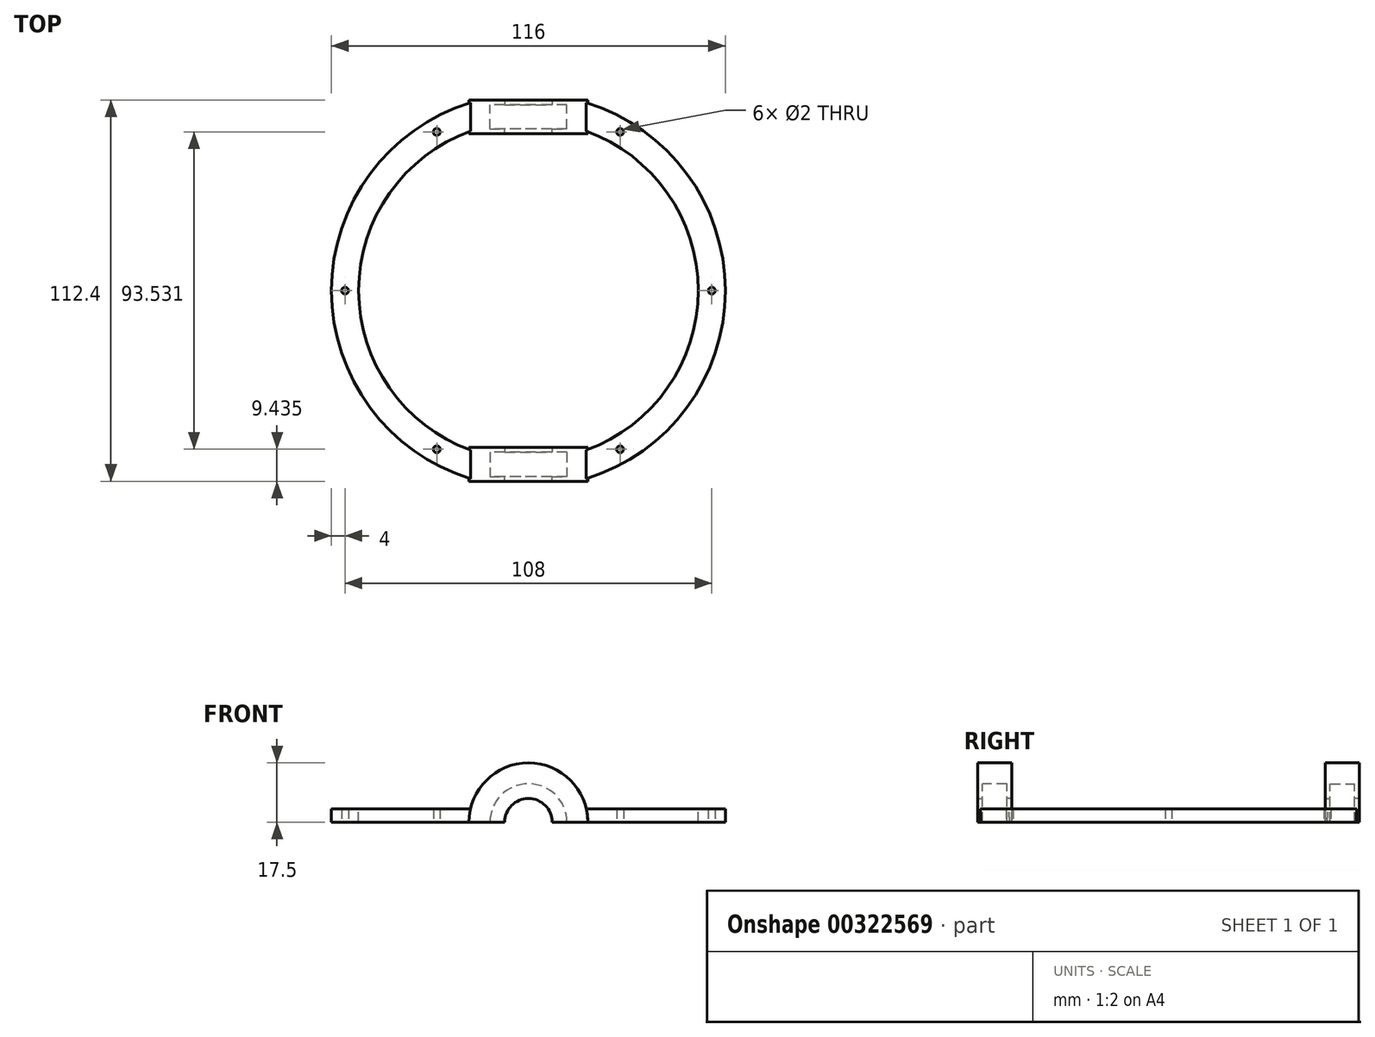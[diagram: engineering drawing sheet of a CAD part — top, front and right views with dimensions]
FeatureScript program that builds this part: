
annotation { "Feature Type Name" : "Feature", "Feature Type Description" : "" }
export const myFeature = defineFeature(function(context is Context, id is Id, definition is map)
    precondition{}
    {
        {
            var Q0;
            Q0=qCreatedBy(makeId("Top.planeOp"),FACE);
            var sketch = newSketch(context, id + "F0", { "sketchPlane" : qUnion([Q0])});
            skCircle(sketch, "E0", {"center": v(0, 0) * mm, "radius": 50 * mm});
            skCircle(sketch, "E1", {"center": v(0, 0) * mm, "radius": 58 * mm});
            skSolve(sketch);
        }
        {
            var Q0;
            Q0=qSketchRegion(id+"F0",true);
            extrude(context, id + "F1", {"entities" : qUnion([Q0]), "depth" : 4 * mm, "hasSecondDirection" : true, "secondDirectionOppositeDirection" : true, "secondDirectionDepth" : 4 * mm});
        }
        {
            var Q0;
            Q0=qCreatedBy(makeId("Front.planeOp"),FACE);
            cPlane(context, id + "F2", {"entities" : qUnion([Q0]), "cplaneType" : CPlaneType.OFFSET, "offset" : 54.8 * mm, "width" : 150 * mm, "height" : 150 * mm});
        }
        {
            var Q0;
            Q0=qCreatedBy(id+"F2.planeOp",FACE);
            var sketch = newSketch(context, id + "F3", { "sketchPlane" : qUnion([Q0])});
            skCircle(sketch, "E2", {"center": v(0, 0) * mm, "radius": 11.35 * mm});
            skCircle(sketch, "E3", {"center": v(0, 0) * mm, "radius": 17.5 * mm});
            skSolve(sketch);
        }
        {
            var Q0;
            Q0=makeQuery(id+"F3.imprint","IMPRINT",FACE,{"disambiguationData":[TD([[makeQuery(id+"F3.imprint","IMPRINT",EDGE,{"derivedFrom":sQuery(id+"F3.wireOp",EDGE,"E2")}),1.0]])]});
            var Q1;
            Q1=makeQuery(id+"F3.imprint","IMPRINT",FACE,{"disambiguationData":[TD([[makeQuery(id+"F3.imprint","IMPRINT",EDGE,{"derivedFrom":sQuery(id+"F3.wireOp",EDGE,"E2")}),-1.0]])]});
            extrude(context, id + "F4", {"entities" : qUnion([Q0, Q1]), "operationType" : NewBodyOperationType.REMOVE, "oppositeDirection" : true, "depth" : 25 * mm, "hasSecondDirection" : true, "secondDirectionOppositeDirection" : false, "secondDirectionDepth" : 25 * mm});
        }
        {
            var Q0;
            Q0=makeQuery(id+"F3.imprint","IMPRINT",FACE,{"disambiguationData":[TD([[makeQuery(id+"F3.imprint","IMPRINT",EDGE,{"derivedFrom":sQuery(id+"F3.wireOp",EDGE,"E2")}),-1.0]])]});
            extrude(context, id + "F5", {"entities" : qUnion([Q0]), "operationType" : NewBodyOperationType.ADD, "oppositeDirection" : true, "depth" : 7.2 * mm});
        }
        {
            var Q0;
            Q0=makeQuery(id+"F5.opExtrude","CAP_FACE",FACE,{"disambiguationData":[OSD([sQuery(id+"F3.wireOp",EDGE,"E2"),sQuery(id+"F3.wireOp",EDGE,"E3")])],"isStart":true});
            var sketch = newSketch(context, id + "F6", { "sketchPlane" : qUnion([Q0])});
            skCircle(sketch, "E4", {"center": v(0, 0) * mm, "radius": 7 * mm});
            skCircle(sketch, "E5", {"center": v(0, 0) * mm, "radius": 17.5 * mm});
            skSolve(sketch);
        }
        {
            var Q0;
            Q0=makeQuery(id+"F6.imprint","IMPRINT",FACE,{"disambiguationData":[TD([[makeQuery(id+"F6.imprint","IMPRINT",EDGE,{"derivedFrom":sQuery(id+"F6.wireOp",EDGE,"E4")}),-1.0]])]});
            var Q1;
            Q1=makeQuery(id+"F6.imprint","IMPRINT",FACE,{"disambiguationData":[TD([[makeQuery(id+"F6.imprint","IMPRINT",EDGE,{"derivedFrom":sQuery(id+"F6.wireOp",EDGE,"E5")}),1.0]])]});
            extrude(context, id + "F7", {"entities" : qUnion([Q0, Q1]), "operationType" : NewBodyOperationType.ADD, "depth" : 1.4 * mm});
        }
        {
            var Q0;
            Q0=makeQuery(id+"F5.opExtrude","CAP_FACE",FACE,{"disambiguationData":[OSD([sQuery(id+"F3.wireOp",EDGE,"E2"),sQuery(id+"F3.wireOp",EDGE,"E3")])],"isStart":false});
            var sketch = newSketch(context, id + "F8", { "sketchPlane" : qUnion([Q0])});
            skCircle(sketch, "E6", {"center": v(0, 0) * mm, "radius": 7 * mm});
            skCircle(sketch, "E7", {"center": v(0, 0) * mm, "radius": 17.5 * mm});
            skSolve(sketch);
        }
        {
            var Q0;
            Q0=makeQuery(id+"F8.imprint","IMPRINT",FACE,{"disambiguationData":[TD([[makeQuery(id+"F8.imprint","IMPRINT",EDGE,{"derivedFrom":sQuery(id+"F8.wireOp",EDGE,"E7")}),-1.0]])]});
            var Q1;
            Q1=makeQuery(id+"F8.imprint","IMPRINT",FACE,{"disambiguationData":[TD([[makeQuery(id+"F8.imprint","IMPRINT",EDGE,{"derivedFrom":sQuery(id+"F8.wireOp",EDGE,"E6")}),-1.0]])]});
            extrude(context, id + "F9", {"entities" : qUnion([Q0, Q1]), "operationType" : NewBodyOperationType.ADD, "depth" : 1.4 * mm});
        }
        {
            var Q0;
            Q0=qCreatedBy(makeId("Front.planeOp"),FACE);
            cPlane(context, id + "F10", {"entities" : qUnion([Q0]), "cplaneType" : CPlaneType.OFFSET, "offset" : 54.8 * mm, "oppositeDirection" : true, "width" : 150 * mm, "height" : 150 * mm});
        }
        {
            var Q0;
            Q0=qCreatedBy(id+"F10.planeOp",FACE);
            var sketch = newSketch(context, id + "F11", { "sketchPlane" : qUnion([Q0])});
            skCircle(sketch, "E8", {"center": v(0, 0) * mm, "radius": 17.5 * mm});
            skCircle(sketch, "E9", {"center": v(0, 0) * mm, "radius": 11.35 * mm});
            skSolve(sketch);
        }
        {
            var Q0;
            Q0=makeQuery(id+"F11.imprint","IMPRINT",FACE,{"disambiguationData":[TD([[makeQuery(id+"F11.imprint","IMPRINT",EDGE,{"derivedFrom":sQuery(id+"F11.wireOp",EDGE,"E8")}),1.0]])]});
            var Q1;
            Q1=makeQuery(id+"F11.imprint","IMPRINT",FACE,{"disambiguationData":[TD([[makeQuery(id+"F11.imprint","IMPRINT",EDGE,{"derivedFrom":sQuery(id+"F11.wireOp",EDGE,"E9")}),1.0]])]});
            extrude(context, id + "F12", {"entities" : qUnion([Q0, Q1]), "operationType" : NewBodyOperationType.REMOVE, "depth" : 25 * mm, "hasSecondDirection" : true, "secondDirectionOppositeDirection" : true, "secondDirectionDepth" : 25 * mm});
        }
        {
            var Q0;
            Q0=makeQuery(id+"F11.imprint","IMPRINT",FACE,{"disambiguationData":[TD([[makeQuery(id+"F11.imprint","IMPRINT",EDGE,{"derivedFrom":sQuery(id+"F11.wireOp",EDGE,"E8")}),1.0]])]});
            extrude(context, id + "F13", {"entities" : qUnion([Q0]), "operationType" : NewBodyOperationType.ADD, "depth" : 7.2 * mm});
        }
        {
            var Q0;
            Q0=makeQuery(id+"F13.opExtrude","CAP_FACE",FACE,{"disambiguationData":[OSD([sQuery(id+"F11.wireOp",EDGE,"E8"),sQuery(id+"F11.wireOp",EDGE,"E9")])],"isStart":true});
            var sketch = newSketch(context, id + "F14", { "sketchPlane" : qUnion([Q0])});
            skCircle(sketch, "E10", {"center": v(0, 0) * mm, "radius": 7 * mm});
            skCircle(sketch, "E11", {"center": v(0, 0) * mm, "radius": 17.5 * mm});
            skSolve(sketch);
        }
        {
            var Q0;
            Q0=makeQuery(id+"F14.imprint","IMPRINT",FACE,{"disambiguationData":[TD([[makeQuery(id+"F14.imprint","IMPRINT",EDGE,{"derivedFrom":makeQuery(id+"F13.opExtrude","CAP_EDGE",EDGE,{"disambiguationData":[OSD([sQuery(id+"F11.wireOp",EDGE,"E9")])],"isStart":true})}),1.0]])]});
            var Q1;
            Q1=makeQuery(id+"F14.imprint","IMPRINT",FACE,{"disambiguationData":[TD([[makeQuery(id+"F14.imprint","IMPRINT",EDGE,{"derivedFrom":sQuery(id+"F14.wireOp",EDGE,"E10")}),-1.0]])]});
            extrude(context, id + "F15", {"entities" : qUnion([Q0, Q1]), "operationType" : NewBodyOperationType.ADD, "depth" : 1.4 * mm});
        }
        {
            var Q0;
            Q0=makeQuery(id+"F13.opExtrude","CAP_FACE",FACE,{"disambiguationData":[OSD([sQuery(id+"F11.wireOp",EDGE,"E8"),sQuery(id+"F11.wireOp",EDGE,"E9")])],"isStart":false});
            var sketch = newSketch(context, id + "F16", { "sketchPlane" : qUnion([Q0])});
            skCircle(sketch, "E12", {"center": v(0, 0) * mm, "radius": 7 * mm});
            skCircle(sketch, "E13", {"center": v(0, 0) * mm, "radius": 17.5 * mm});
            skSolve(sketch);
        }
        {
            var Q0;
            Q0=makeQuery(id+"F16.imprint","IMPRINT",FACE,{"disambiguationData":[TD([[makeQuery(id+"F16.imprint","IMPRINT",EDGE,{"derivedFrom":sQuery(id+"F16.wireOp",EDGE,"E12")}),-1.0]])]});
            var Q1;
            Q1=makeQuery(id+"F16.imprint","IMPRINT",FACE,{"disambiguationData":[TD([[makeQuery(id+"F16.imprint","IMPRINT",EDGE,{"derivedFrom":sQuery(id+"F16.wireOp",EDGE,"E13")}),1.0]])]});
            extrude(context, id + "F17", {"entities" : qUnion([Q0, Q1]), "operationType" : NewBodyOperationType.ADD, "depth" : 1.4 * mm});
        }
        {
            var Q0;
            Q0=makeQuery(id+"F12.boolean.opBoolean","SPLIT",FACE,{"disambiguationData":[OD(0.0)],"derivedFrom":makeQuery(id+"F1.opExtrude","CAP_FACE",FACE,{"disambiguationData":[OSD([sQuery(id+"F0.wireOp",EDGE,"E0"),sQuery(id+"F0.wireOp",EDGE,"E1")])],"isStart":false})});
            var sketch = newSketch(context, id + "F18", { "sketchPlane" : qUnion([Q0])});
            skLineSegment(sketch, "E14", {"start": v(0, 0) * mm, "end": v(-50, 0) * mm, "construction": true});
            skLineSegment(sketch, "E15", {"start": v(-50, 0) * mm, "end": v(-58, 0) * mm, "construction": true});
            skCircle(sketch, "E16", {"center": v(-54, 0) * mm, "radius": 3 * mm});
            skCircle(sketch, "E17", {"center": v(-54, 0) * mm, "radius": 1.5 * mm});
            skCircle(sketch, "E18", {"center": v(-54, 0) * mm, "radius": 1 * mm});
            skCircle(sketch, "E19.1.0", {"center": v(-27, -46.77) * mm, "radius": 3 * mm});
            skCircle(sketch, "E19.1.1", {"center": v(-27, -46.77) * mm, "radius": 1.5 * mm});
            skCircle(sketch, "E19.1.2", {"center": v(-27, -46.77) * mm, "radius": 1 * mm});
            skCircle(sketch, "E19.2.0", {"center": v(27, -46.77) * mm, "radius": 3 * mm});
            skCircle(sketch, "E19.2.1", {"center": v(27, -46.77) * mm, "radius": 1.5 * mm});
            skCircle(sketch, "E19.2.2", {"center": v(27, -46.77) * mm, "radius": 1 * mm});
            skCircle(sketch, "E19.3.0", {"center": v(54, 0) * mm, "radius": 3 * mm});
            skCircle(sketch, "E19.3.1", {"center": v(54, 0) * mm, "radius": 1.5 * mm});
            skCircle(sketch, "E19.3.2", {"center": v(54, 0) * mm, "radius": 1 * mm});
            skCircle(sketch, "E19.4.0", {"center": v(27, 46.77) * mm, "radius": 3 * mm});
            skCircle(sketch, "E19.4.1", {"center": v(27, 46.77) * mm, "radius": 1.5 * mm});
            skCircle(sketch, "E19.4.2", {"center": v(27, 46.77) * mm, "radius": 1 * mm});
            skCircle(sketch, "E19.5.0", {"center": v(-27, 46.77) * mm, "radius": 3 * mm});
            skCircle(sketch, "E19.5.1", {"center": v(-27, 46.77) * mm, "radius": 1.5 * mm});
            skCircle(sketch, "E19.5.2", {"center": v(-27, 46.77) * mm, "radius": 1 * mm});
            skPoint(sketch, "E19.center", {"position": v(0, 0) * mm});
            skSolve(sketch);
        }
        {
            var Q0;
            Q0=makeQuery(id+"F18.imprint","IMPRINT",FACE,{"disambiguationData":[TD([[makeQuery(id+"F18.imprint","IMPRINT",EDGE,{"derivedFrom":sQuery(id+"F18.wireOp",EDGE,"E18")}),1.0]])]});
            var Q1;
            Q1=makeQuery(id+"F18.imprint","IMPRINT",FACE,{"disambiguationData":[TD([[makeQuery(id+"F18.imprint","IMPRINT",EDGE,{"derivedFrom":sQuery(id+"F18.wireOp",EDGE,"E19.5.2")}),1.0]])]});
            var Q2;
            Q2=makeQuery(id+"F18.imprint","IMPRINT",FACE,{"disambiguationData":[TD([[makeQuery(id+"F18.imprint","IMPRINT",EDGE,{"derivedFrom":sQuery(id+"F18.wireOp",EDGE,"E19.4.2")}),1.0]])]});
            var Q3;
            Q3=makeQuery(id+"F18.imprint","IMPRINT",FACE,{"disambiguationData":[TD([[makeQuery(id+"F18.imprint","IMPRINT",EDGE,{"derivedFrom":sQuery(id+"F18.wireOp",EDGE,"E19.3.2")}),1.0]])]});
            var Q4;
            Q4=makeQuery(id+"F18.imprint","IMPRINT",FACE,{"disambiguationData":[TD([[makeQuery(id+"F18.imprint","IMPRINT",EDGE,{"derivedFrom":sQuery(id+"F18.wireOp",EDGE,"E19.2.2")}),1.0]])]});
            var Q5;
            Q5=makeQuery(id+"F18.imprint","IMPRINT",FACE,{"disambiguationData":[TD([[makeQuery(id+"F18.imprint","IMPRINT",EDGE,{"derivedFrom":sQuery(id+"F18.wireOp",EDGE,"E19.1.2")}),1.0]])]});
            extrude(context, id + "F19", {"entities" : qUnion([Q0, Q1, Q2, Q3, Q4, Q5]), "operationType" : NewBodyOperationType.REMOVE, "oppositeDirection" : true, "depth" : 25 * mm});
        }
        {
            var Q0;
            Q0=makeQuery(id+"F18.imprint","IMPRINT",FACE,{"disambiguationData":[TD([[makeQuery(id+"F18.imprint","IMPRINT",EDGE,{"derivedFrom":sQuery(id+"F18.wireOp",EDGE,"E17")}),1.0]])]});
            var Q1;
            Q1=makeQuery(id+"F18.imprint","IMPRINT",FACE,{"disambiguationData":[TD([[makeQuery(id+"F18.imprint","IMPRINT",EDGE,{"derivedFrom":sQuery(id+"F18.wireOp",EDGE,"E19.5.1")}),1.0]])]});
            var Q2;
            Q2=makeQuery(id+"F18.imprint","IMPRINT",FACE,{"disambiguationData":[TD([[makeQuery(id+"F18.imprint","IMPRINT",EDGE,{"derivedFrom":sQuery(id+"F18.wireOp",EDGE,"E19.4.1")}),1.0]])]});
            var Q3;
            Q3=makeQuery(id+"F18.imprint","IMPRINT",FACE,{"disambiguationData":[TD([[makeQuery(id+"F18.imprint","IMPRINT",EDGE,{"derivedFrom":sQuery(id+"F18.wireOp",EDGE,"E19.3.1")}),1.0]])]});
            var Q4;
            Q4=makeQuery(id+"F18.imprint","IMPRINT",FACE,{"disambiguationData":[TD([[makeQuery(id+"F18.imprint","IMPRINT",EDGE,{"derivedFrom":sQuery(id+"F18.wireOp",EDGE,"E19.2.1")}),1.0]])]});
            var Q5;
            Q5=makeQuery(id+"F18.imprint","IMPRINT",FACE,{"disambiguationData":[TD([[makeQuery(id+"F18.imprint","IMPRINT",EDGE,{"derivedFrom":sQuery(id+"F18.wireOp",EDGE,"E19.1.1")}),1.0]])]});
            extrude(context, id + "F20", {"entities" : qUnion([Q0, Q1, Q2, Q3, Q4, Q5]), "operationType" : NewBodyOperationType.REMOVE, "oppositeDirection" : true, "depth" : 4 * mm});
        }
        {
            var Q0;
            Q0=makeQuery(id+"F18.imprint","IMPRINT",FACE,{"disambiguationData":[TD([[makeQuery(id+"F18.imprint","IMPRINT",EDGE,{"derivedFrom":sQuery(id+"F18.wireOp",EDGE,"E16")}),1.0]])]});
            var Q1;
            Q1=makeQuery(id+"F18.imprint","IMPRINT",FACE,{"disambiguationData":[TD([[makeQuery(id+"F18.imprint","IMPRINT",EDGE,{"derivedFrom":sQuery(id+"F18.wireOp",EDGE,"E19.1.0")}),1.0]])]});
            var Q2;
            Q2=makeQuery(id+"F18.imprint","IMPRINT",FACE,{"disambiguationData":[TD([[makeQuery(id+"F18.imprint","IMPRINT",EDGE,{"derivedFrom":sQuery(id+"F18.wireOp",EDGE,"E19.2.0")}),1.0]])]});
            var Q3;
            Q3=makeQuery(id+"F18.imprint","IMPRINT",FACE,{"disambiguationData":[TD([[makeQuery(id+"F18.imprint","IMPRINT",EDGE,{"derivedFrom":sQuery(id+"F18.wireOp",EDGE,"E19.3.0")}),1.0]])]});
            var Q4;
            Q4=makeQuery(id+"F18.imprint","IMPRINT",FACE,{"disambiguationData":[TD([[makeQuery(id+"F18.imprint","IMPRINT",EDGE,{"derivedFrom":sQuery(id+"F18.wireOp",EDGE,"E19.4.0")}),1.0]])]});
            var Q5;
            Q5=makeQuery(id+"F18.imprint","IMPRINT",FACE,{"disambiguationData":[TD([[makeQuery(id+"F18.imprint","IMPRINT",EDGE,{"derivedFrom":sQuery(id+"F18.wireOp",EDGE,"E19.5.0")}),1.0]])]});
            extrude(context, id + "F21", {"entities" : qUnion([Q0, Q1, Q2, Q3, Q4, Q5]), "operationType" : NewBodyOperationType.REMOVE, "oppositeDirection" : true, "depth" : 2 * mm});
        }
        {
            var Q0;
            Q0=qCreatedBy(makeId("Top.planeOp"),FACE);
            var sketch = newSketch(context, id + "F22", { "sketchPlane" : qUnion([Q0])});
            skCircle(sketch, "E20", {"center": v(0, 0) * mm, "radius": 78.22 * mm});
            skSolve(sketch);
        }
        {
            var Q0;
            Q0 = qSketchRegion(id + "F22", true);
            extrude(context, id + "F23", {"entities" : qUnion([Q0]), "operationType" : NewBodyOperationType.REMOVE, "depth" : 25 * mm});
        }
        {
            var Q0;
            Q0=qCreatedBy(makeId("Top.planeOp"),FACE);
            var sketch = newSketch(context, id + "F24", { "sketchPlane" : qUnion([Q0])});
            skLineSegment(sketch, "E21", {"start": v(0, 0) * mm, "end": v(0, 16.85) * mm, "construction": true});
            skSolve(sketch);
        }
        {
            var Q0;
            Q0=makeQuery(id+"F1.opExtrude","SWEPT_BODY",BODY,{"disambiguationData":[OSD([sQuery(id+"F0.wireOp",EDGE,"E0"),sQuery(id+"F0.wireOp",EDGE,"E1")])]});
            var Q1;
            Q1=sQuery(id+"F24.wireOp",EDGE,"E21");
            transform(context, id + "F25", {"entities" : qUnion([Q0]), "transformType" : TransformType.ROTATION, "transformAxis" : qUnion([Q1]), "angle" : 180 * degree, "makeCopy" : false});
        }
    });
